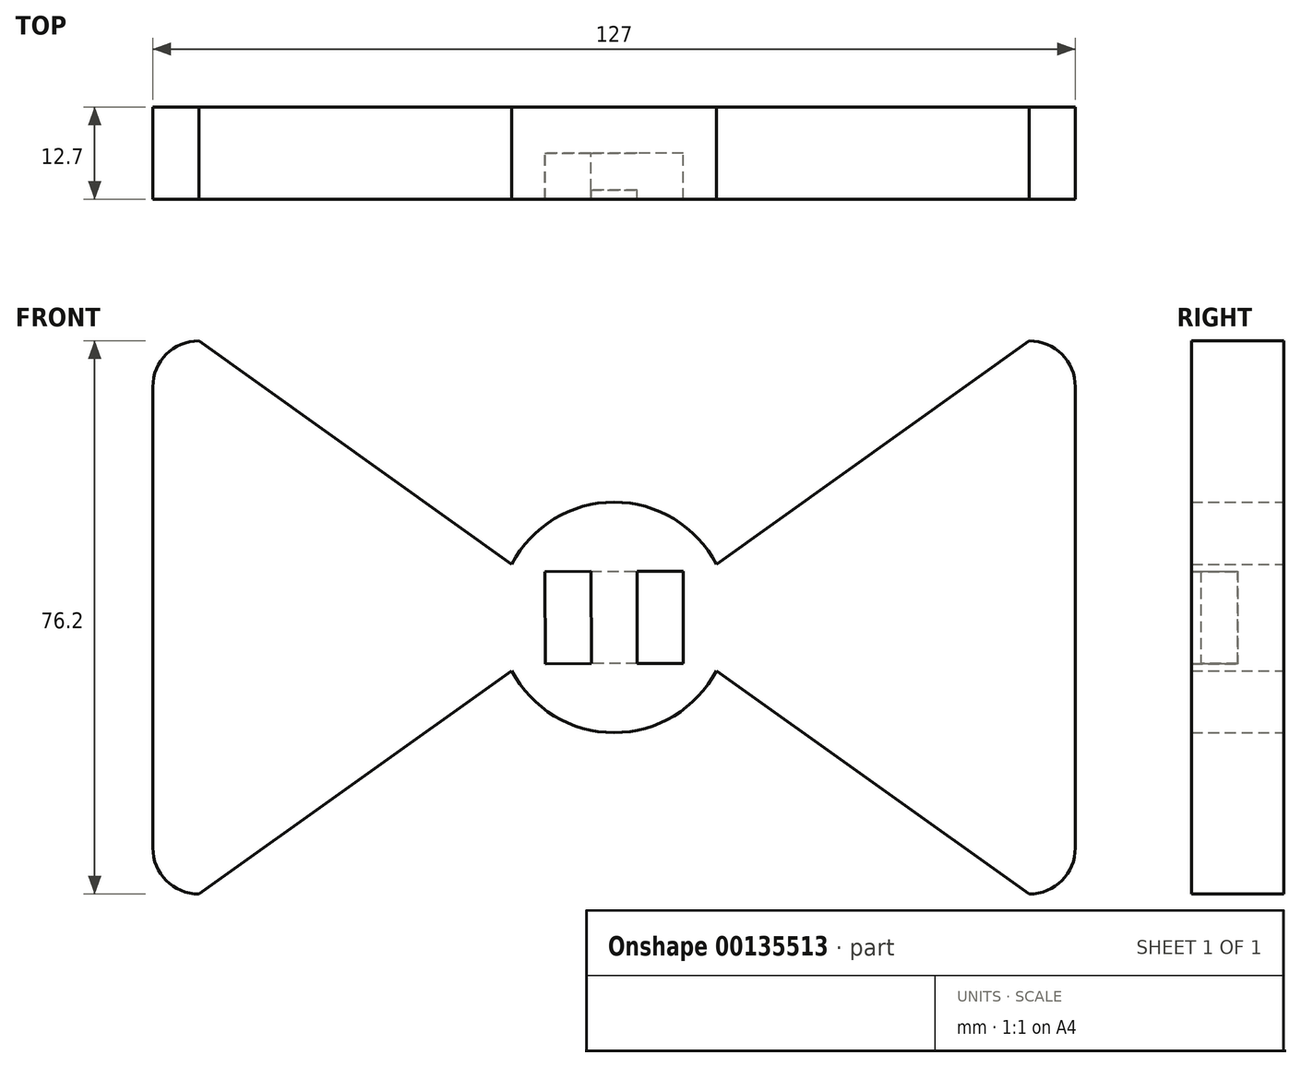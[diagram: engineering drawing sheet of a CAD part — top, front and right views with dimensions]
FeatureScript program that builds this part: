
annotation { "Feature Type Name" : "Feature", "Feature Type Description" : "" }
export const myFeature = defineFeature(function(context is Context, id is Id, definition is map)
    precondition{}
    {
        {
            var Q0;
            Q0=qCreatedBy(makeId("Front.planeOp"),FACE);
            var sketch = newSketch(context, id + "F0", { "sketchPlane" : qUnion([Q0])});
            skPoint(sketch, "E0.middle", {"position": v(0, 0) * mm});
            skPoint(sketch, "E1.endSnap0", {"position": v(12.7, 0) * mm});
            skPoint(sketch, "E2.endSnap0", {"position": v(-12.7, 0) * mm});
            skLineSegment(sketch, "E3", {"start": v(-63.5, 0) * mm, "end": v(-63.5, -31.75) * mm});
            skLineSegment(sketch, "E4", {"start": v(-63.5, 0) * mm, "end": v(-63.5, 31.75) * mm});
            skLineSegment(sketch, "E5", {"start": v(63.5, 0) * mm, "end": v(63.5, -31.75) * mm});
            skLineSegment(sketch, "E6", {"start": v(63.5, 0) * mm, "end": v(63.5, 31.75) * mm});
            skLineSegment(sketch, "E7", {"start": v(-57.15, -38.1) * mm, "end": v(-14.08, -7.33) * mm});
            skLineSegment(sketch, "E8", {"start": v(-57.15, 38.1) * mm, "end": v(-14.08, 7.33) * mm});
            skLineSegment(sketch, "E9", {"start": v(14.08, -7.33) * mm, "end": v(57.15, -38.1) * mm});
            skLineSegment(sketch, "E10", {"start": v(57.15, 38.1) * mm, "end": v(14.08, 7.33) * mm});
            skArc(sketch, "E11", {"start": v(-63.5, 31.75) * mm, "mid": v(-61.64, 36.24) * mm, "end": v(-57.15, 38.1) * mm});
            skArc(sketch, "E12", {"start": v(-63.5, -31.75) * mm, "mid": v(-61.64, -36.24) * mm, "end": v(-57.15, -38.1) * mm});
            skArc(sketch, "E13", {"start": v(63.5, 31.75) * mm, "mid": v(61.64, 36.24) * mm, "end": v(57.15, 38.1) * mm});
            skArc(sketch, "E14", {"start": v(14.08, 7.33) * mm, "mid": v(0, 15.88) * mm, "end": v(-14.08, 7.33) * mm});
            skPoint(sketch, "E15.orphan", {"position": v(-12.7, -12.7) * mm});
            skPoint(sketch, "E16.orphan", {"position": v(12.7, -12.7) * mm});
            skArc(sketch, "E17.trimOffspring", {"start": v(-14.08, -7.33) * mm, "mid": v(0, -15.88) * mm, "end": v(14.08, -7.33) * mm});
            skPoint(sketch, "E18.trimOffspring.end.orphan", {"position": v(-12.7, 12.7) * mm});
            skPoint(sketch, "E19.orphan", {"position": v(12.7, 12.7) * mm});
            skPoint(sketch, "E20.trimOffspring.start.orphan", {"position": v(12.7, 6.35) * mm});
            skArc(sketch, "E21", {"start": v(63.5, -31.75) * mm, "mid": v(61.64, -36.24) * mm, "end": v(57.15, -38.1) * mm});
            skSolve(sketch);
        }
        {
            var Q0;
            Q0 = qSketchRegion(id + "F0", true);
            extrude(context, id + "F1", {"entities" : qUnion([Q0]), "depth" : 12.7 * mm});
        }
        {
            var Q0;
            Q0 = qSketchRegion(id + "F0", true);
            extrude(context, id + "F2", {"entities" : qUnion([Q0]), "operationType" : NewBodyOperationType.ADD, "depth" : 12.7 * mm});
        }
        {
            var Q0;
            Q0=qCreatedBy(makeId("Front.planeOp"),FACE);
            cPlane(context, id + "F3", {"entities" : qUnion([Q0]), "cplaneType" : CPlaneType.OFFSET, "offset" : 6.35 * mm, "width" : 152.4 * mm, "height" : 152.4 * mm});
        }
        {
            var Q0;
            Q0=qCreatedBy(id+"F3.planeOp",FACE);
            var sketch = newSketch(context, id + "F4", { "sketchPlane" : qUnion([Q0])});
            skLineSegment(sketch, "E22", {"start": v(3.18, 6.35) * mm, "end": v(3.18, -6.35) * mm});
            skLineSegment(sketch, "E23", {"start": v(3.18, -6.35) * mm, "end": v(9.53, -6.35) * mm});
            skLineSegment(sketch, "E24", {"start": v(9.53, -6.35) * mm, "end": v(9.53, 6.35) * mm});
            skLineSegment(sketch, "E25", {"start": v(9.53, 6.35) * mm, "end": v(3.18, 6.35) * mm});
            skLineSegment(sketch, "E26", {"start": v(-3.17, 6.35) * mm, "end": v(-3.11, -6.35) * mm});
            skLineSegment(sketch, "E27", {"start": v(-3.17, 6.35) * mm, "end": v(-9.52, 6.32) * mm});
            skLineSegment(sketch, "E28", {"start": v(-9.52, 6.32) * mm, "end": v(-9.46, -6.38) * mm});
            skLineSegment(sketch, "E29", {"start": v(-9.46, -6.38) * mm, "end": v(-3.11, -6.35) * mm});
            skSolve(sketch);
        }
        {
            var Q0;
            Q0 = qSketchRegion(id + "F4", true);
            extrude(context, id + "F5", {"entities" : qUnion([Q0]), "operationType" : NewBodyOperationType.REMOVE, "depth" : 25.4 * mm});
        }
        {
            var Q0;
            Q0=qCreatedBy(id+"F3.planeOp",FACE);
            var sketch = newSketch(context, id + "F6", { "sketchPlane" : qUnion([Q0])});
            skLineSegment(sketch, "E30", {"start": v(-3.19, 6.37) * mm, "end": v(3.18, 6.37) * mm});
            skLineSegment(sketch, "E31", {"start": v(3.18, 6.37) * mm, "end": v(3.18, -6.35) * mm});
            skLineSegment(sketch, "E32", {"start": v(3.18, -6.35) * mm, "end": v(-3.12, -6.35) * mm});
            skLineSegment(sketch, "E33", {"start": v(-3.12, -6.35) * mm, "end": v(-3.19, 6.37) * mm});
            skSolve(sketch);
        }
        {
            var Q0;
            Q0 = qSketchRegion(id + "F6", true);
            extrude(context, id + "F7", {"entities" : qUnion([Q0]), "operationType" : NewBodyOperationType.REMOVE, "depth" : 5.08 * mm});
        }
    });
